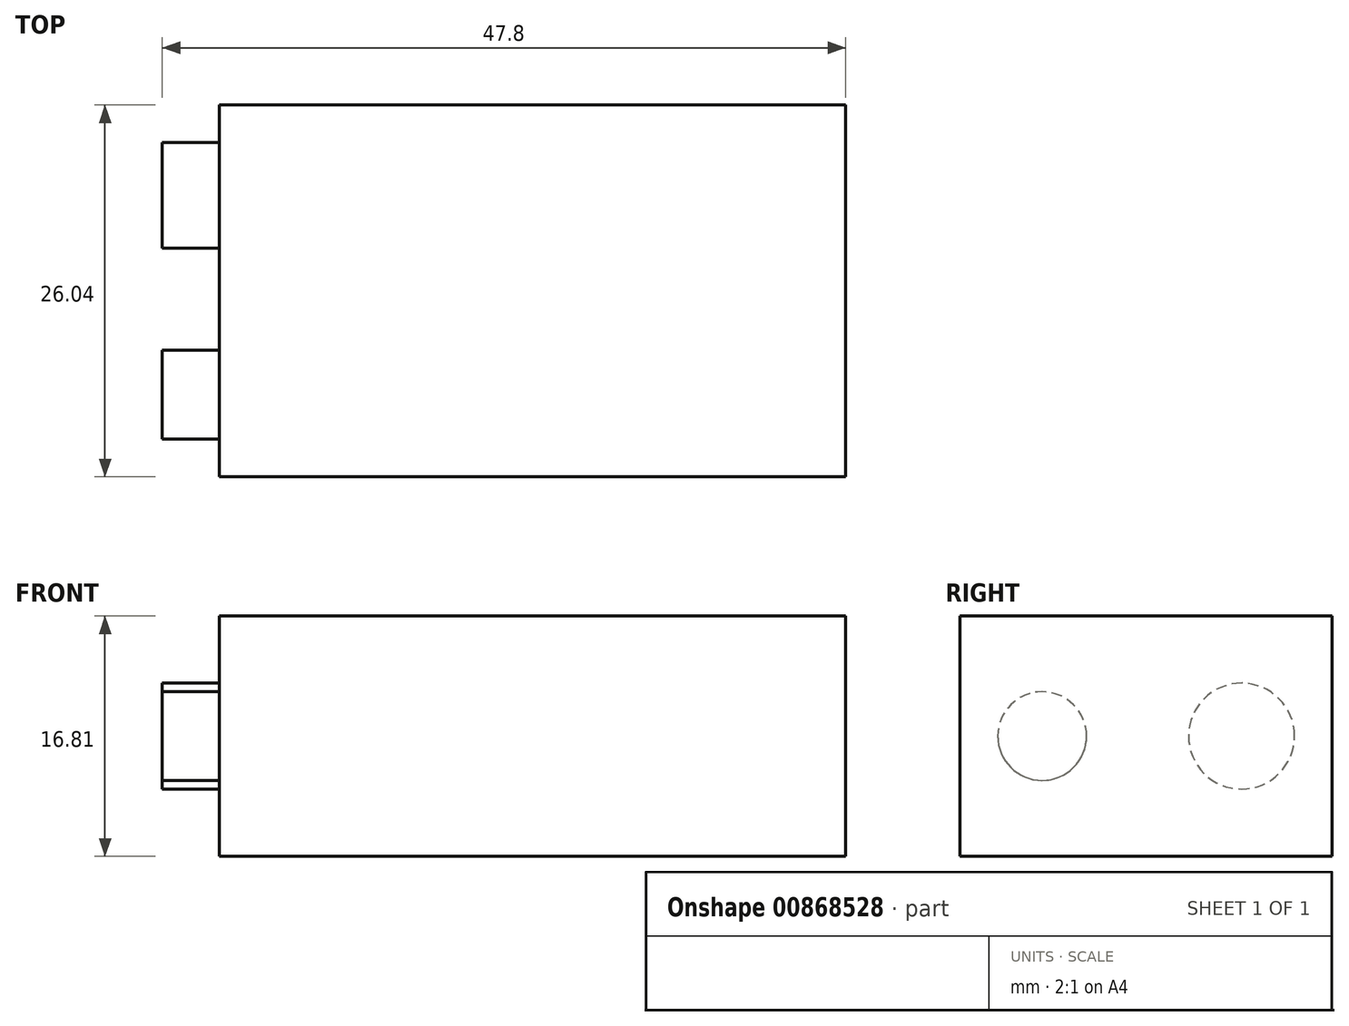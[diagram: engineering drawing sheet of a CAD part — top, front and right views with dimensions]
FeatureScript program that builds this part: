
annotation { "Feature Type Name" : "Feature", "Feature Type Description" : "" }
export const myFeature = defineFeature(function(context is Context, id is Id, definition is map)
    precondition{}
    {
        {
            var Q0;
            Q0=qCreatedBy(makeId("Top.planeOp"),FACE);
            var sketch = newSketch(context, id + "F0", { "sketchPlane" : qUnion([Q0])});
            skLineSegment(sketch, "E0.bottom", {"start": v(3.34, -13.62) * mm, "end": v(47.15, -13.62) * mm});
            skLineSegment(sketch, "E0.top", {"start": v(3.34, -39.66) * mm, "end": v(47.15, -39.66) * mm});
            skLineSegment(sketch, "E0.left", {"start": v(3.34, -13.62) * mm, "end": v(3.34, -39.66) * mm});
            skLineSegment(sketch, "E0.right", {"start": v(47.15, -13.62) * mm, "end": v(47.15, -39.66) * mm});
            skSolve(sketch);
        }
        {
            var Q0;
            Q0 = qSketchRegion(id + "F0", true);
            extrude(context, id + "F1", {"entities" : qUnion([Q0]), "depth" : 16.8 * mm, "offsetDistance" : 25.4 * mm});
        }
        {
            var Q0;
            Q0=makeQuery(id+"F1.opExtrude","SWEPT_FACE",FACE,{"disambiguationData":[OSD([sQuery(id+"F0.wireOp",EDGE,"E0.left")])]});
            var sketch = newSketch(context, id + "F2", { "sketchPlane" : qUnion([Q0])});
            skCircle(sketch, "E1", {"center": v(19.95, 8.4) * mm, "radius": 3.7 * mm});
            skPoint(sketch, "E1.centerSnap0", {"position": v(13.62, 8.4) * mm});
            skCircle(sketch, "E2", {"center": v(33.9, 8.4) * mm, "radius": 3.1 * mm});
            skPoint(sketch, "E2.centerSnap0", {"position": v(39.66, 8.4) * mm});
            skSolve(sketch);
        }
        {
            var Q0;
            Q0 = qSketchRegion(id + "F2", true);
            extrude(context, id + "F3", {"entities" : qUnion([Q0]), "operationType" : NewBodyOperationType.ADD, "depth" : 4 * mm, "offsetDistance" : 25.4 * mm});
        }
    });
